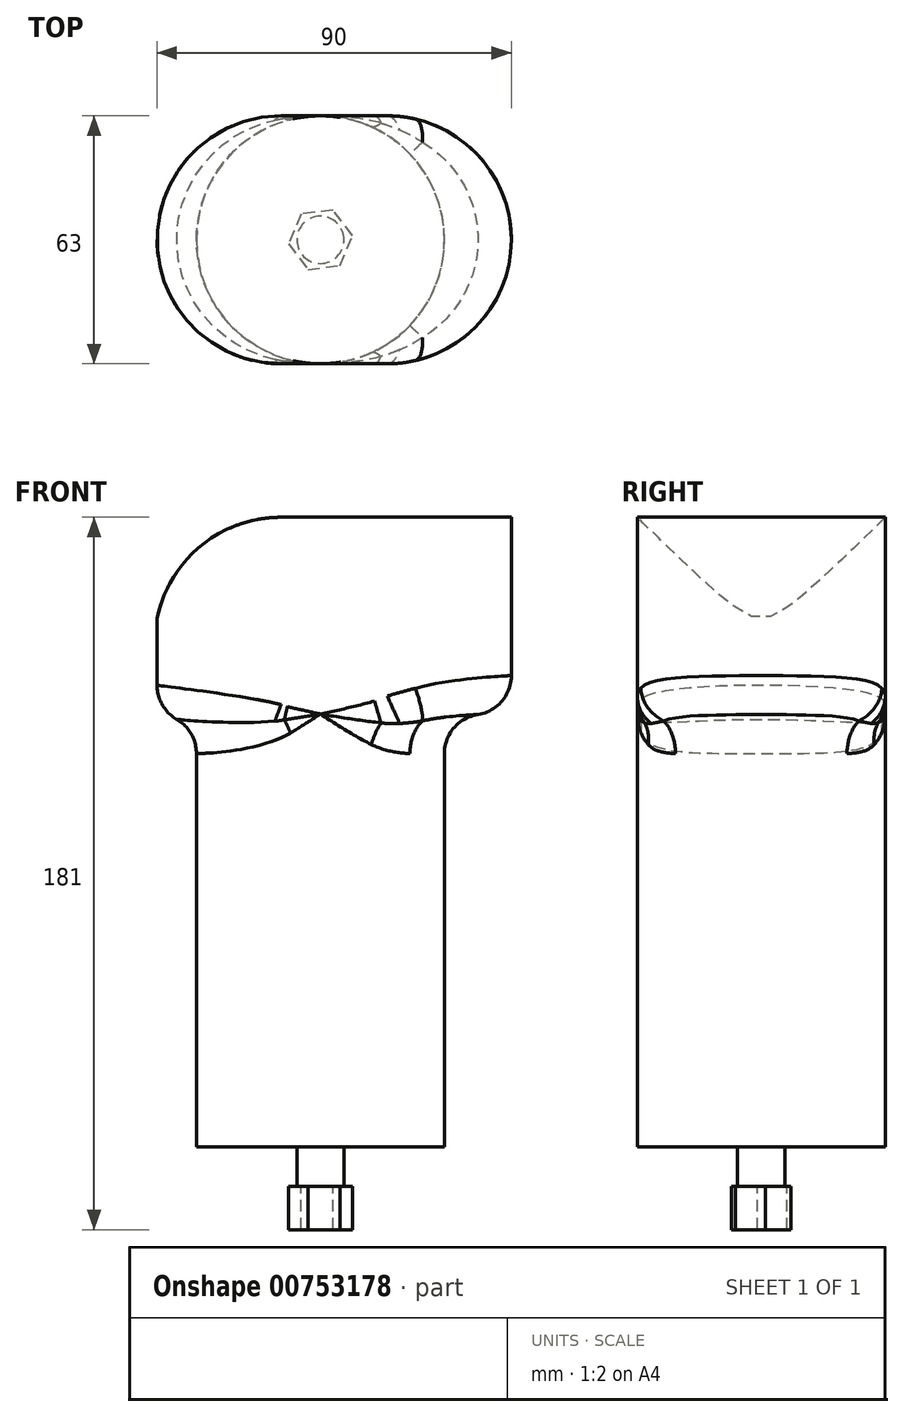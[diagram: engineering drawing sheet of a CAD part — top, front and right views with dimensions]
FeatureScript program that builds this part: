
annotation { "Feature Type Name" : "Feature", "Feature Type Description" : "" }
export const myFeature = defineFeature(function(context is Context, id is Id, definition is map)
    precondition{}
    {
        {
            var Q0;
            Q0=qCreatedBy(makeId("Top.planeOp"),FACE);
            var sketch = newSketch(context, id + "F0", { "sketchPlane" : qUnion([Q0])});
            skCircle(sketch, "E0", {"center": v(158.19, 0) * mm, "radius": 31.5 * mm});
            skSolve(sketch);
        }
        {
            var Q0;
            Q0 = qSketchRegion(id + "F0", true);
            extrude(context, id + "F1", {"entities" : qUnion([Q0]), "depth" : 110 * mm, "offsetDistance" : 25 * mm});
        }
        {
            var Q0;
            Q0=makeQuery(id+"F1.opExtrude","CAP_FACE",FACE,{"disambiguationData":[OSD([sQuery(id+"F0.wireOp",EDGE,"E0")])],"isStart":false});
            var sketch = newSketch(context, id + "F2", { "sketchPlane" : qUnion([Q0])});
            skArc(sketch, "E1", {"start": v(161.69, 28.46) * mm, "mid": v(116.69, 0) * mm, "end": v(161.69, -28.46) * mm});
            skPoint(sketch, "E2", {"position": v(158.19, 0) * mm});
            skArc(sketch, "E3", {"start": v(161.69, -28.46) * mm, "mid": v(206.69, 0) * mm, "end": v(161.69, 28.46) * mm});
            skLineSegment(sketch, "E4", {"start": v(148.19, 31.5) * mm, "end": v(175.19, 31.5) * mm});
            skLineSegment(sketch, "E5", {"start": v(148.19, -31.5) * mm, "end": v(175.19, -31.5) * mm});
            skSolve(sketch);
        }
        {
            var Q0;
            Q0 = qSketchRegion(id + "F2", true);
            extrude(context, id + "F3", {"entities" : qUnion([Q0]), "operationType" : NewBodyOperationType.ADD, "depth" : 50 * mm, "offsetDistance" : 25 * mm});
        }
        {
            var Q0;
            Q0=makeQuery(id+"F3.boolean.opBoolean","SPLIT",EDGE,{"disambiguationData":[OD(0.0)],"derivedFrom":makeQuery(id+"F1.opExtrude","CAP_EDGE",EDGE,{"disambiguationData":[OSD([sQuery(id+"F0.wireOp",EDGE,"E0")])],"isStart":false})});
            fillet(context, id + "F4", {"entities" : qUnion([Q0]), "radius" : 10 * mm, "tangentPropagation" : true, "allowEdgeOverflow" : false});
        }
        {
            var Q0;
            Q0=makeQuery(id+"F4.opFillet","BLEND_EDGE",EDGE,{"blendedFrom":[makeQuery(id+"F3.boolean.opBoolean","SPLIT",EDGE,{"disambiguationData":[OD(0.0)],"derivedFrom":makeQuery(id+"F1.opExtrude","CAP_EDGE",EDGE,{"disambiguationData":[OSD([sQuery(id+"F0.wireOp",EDGE,"E0")])],"isStart":false})}),makeQuery(id+"F3.opExtrude","SWEPT_FACE",FACE,{"disambiguationData":[OSD([sQuery(id+"F2.wireOp",EDGE,"E1")])]})],"blendedInto":[makeQuery(id+"F3.opExtrude","SWEPT_FACE",FACE,{"disambiguationData":[OSD([sQuery(id+"F2.wireOp",EDGE,"E1")])]})]});
            var Q1;
            Q1=makeQuery(id+"F3.opExtrude","CAP_EDGE",EDGE,{"disambiguationData":[OSD([sQuery(id+"F2.wireOp",EDGE,"E3")])],"isStart":true});
            fillet(context, id + "F5", {"entities" : qUnion([Q0, Q1]), "radius" : 10 * mm, "tangentPropagation" : true, "allowEdgeOverflow" : false});
        }
        {
            var Q0;
            Q0=makeQuery(id+"F3.opExtrude","SWEPT_FACE",FACE,{"disambiguationData":[OSD([sQuery(id+"F2.wireOp",EDGE,"E5")])]});
            var sketch = newSketch(context, id + "F6", { "sketchPlane" : qUnion([Q0])});
            skArc(sketch, "E6", {"start": v(148.19, 160) * mm, "mid": v(127.88, 152.78) * mm, "end": v(116.69, 134.36) * mm});
            skLineSegment(sketch, "E7", {"start": v(116.69, 160) * mm, "end": v(148.19, 160) * mm});
            skLineSegment(sketch, "E8", {"start": v(116.69, 134.36) * mm, "end": v(116.69, 160) * mm});
            skSolve(sketch);
        }
        {
            var Q0;
            Q0 = qSketchRegion(id + "F6", true);
            extrude(context, id + "F7", {"entities" : qUnion([Q0]), "operationType" : NewBodyOperationType.REMOVE, "endBound" : BoundingType.THROUGH_ALL, "oppositeDirection" : true, "depth" : 25 * mm, "offsetDistance" : 25 * mm});
        }
        {
            var Q0;
            Q0=makeQuery(id+"F1.opExtrude","CAP_FACE",FACE,{"disambiguationData":[OSD([sQuery(id+"F0.wireOp",EDGE,"E0")])],"isStart":true});
            var sketch = newSketch(context, id + "F8", { "sketchPlane" : qUnion([Q0])});
            skCircle(sketch, "E9", {"center": v(158.19, 0) * mm, "radius": 6 * mm});
            skSolve(sketch);
        }
        {
            var Q0;
            Q0 = qSketchRegion(id + "F8", true);
            extrude(context, id + "F9", {"entities" : qUnion([Q0]), "operationType" : NewBodyOperationType.ADD, "depth" : 10 * mm, "offsetDistance" : 25 * mm});
        }
        {
            var Q0;
            Q0=makeQuery(id+"F9.opExtrude","CAP_FACE",FACE,{"disambiguationData":[OSD([sQuery(id+"F8.wireOp",EDGE,"E9")])],"isStart":false});
            var sketch = newSketch(context, id + "F10", { "sketchPlane" : qUnion([Q0])});
            skCircle(sketch, "E10.cCircle", {"center": v(158.19, 0) * mm, "radius": 7.1 * mm, "construction": true});
            skLineSegment(sketch, "E10.0", {"start": v(166.33, -1.03) * mm, "end": v(161.37, -7.56) * mm});
            skLineSegment(sketch, "E10.1", {"start": v(161.37, -7.56) * mm, "end": v(153.23, -6.53) * mm});
            skLineSegment(sketch, "E10.2", {"start": v(153.23, -6.53) * mm, "end": v(150.05, 1.03) * mm});
            skLineSegment(sketch, "E10.3", {"start": v(150.05, 1.03) * mm, "end": v(155, 7.56) * mm});
            skLineSegment(sketch, "E10.4", {"start": v(155, 7.56) * mm, "end": v(163.15, 6.53) * mm});
            skLineSegment(sketch, "E10.5", {"start": v(163.15, 6.53) * mm, "end": v(166.33, -1.03) * mm});
            skPoint(sketch, "E10.0.midPoint", {"position": v(163.85, -4.3) * mm});
            skSolve(sketch);
        }
        {
            var Q0;
            Q0 = qSketchRegion(id + "F10", true);
            extrude(context, id + "F11", {"entities" : qUnion([Q0]), "operationType" : NewBodyOperationType.ADD, "depth" : 11 * mm, "offsetDistance" : 25 * mm});
        }
    });
